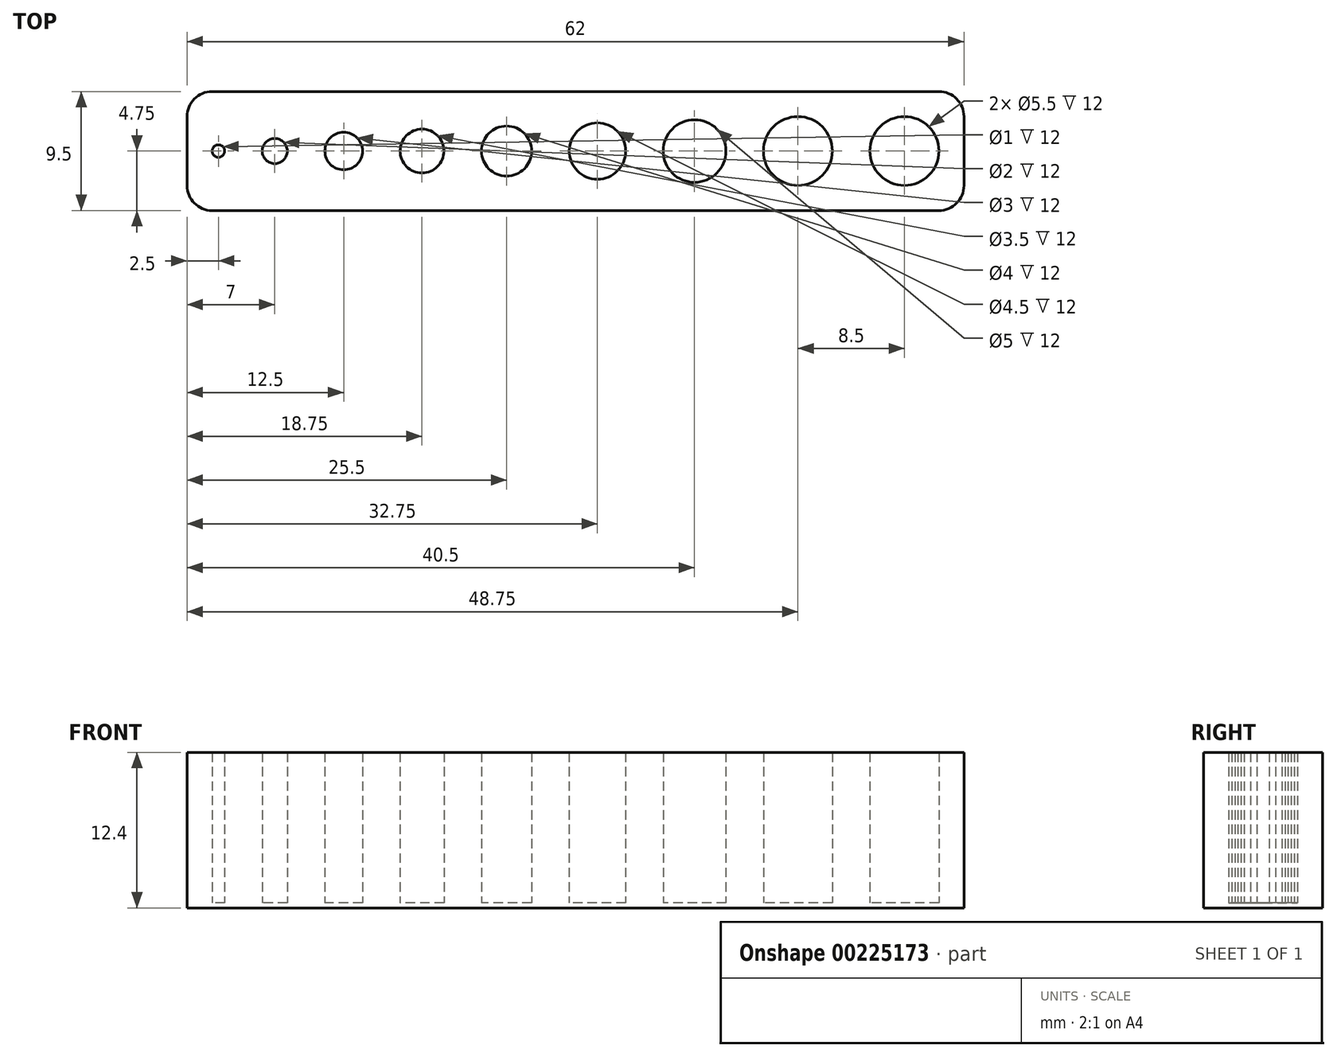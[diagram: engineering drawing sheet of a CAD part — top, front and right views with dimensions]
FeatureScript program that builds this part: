
annotation { "Feature Type Name" : "Feature", "Feature Type Description" : "" }
export const myFeature = defineFeature(function(context is Context, id is Id, definition is map)
    precondition{}
    {
        {
            var Q0;
            Q0=qCreatedBy(makeId("Top.planeOp"),FACE);
            var sketch = newSketch(context, id + "F0", { "sketchPlane" : qUnion([Q0])});
            skLineSegment(sketch, "E0.bottom", {"start": v(29.25, -4.75) * mm, "end": v(-32.75, -4.75) * mm});
            skLineSegment(sketch, "E0.top", {"start": v(29.25, 4.75) * mm, "end": v(-32.75, 4.75) * mm});
            skLineSegment(sketch, "E0.left", {"start": v(29.25, -4.75) * mm, "end": v(29.25, 4.75) * mm});
            skLineSegment(sketch, "E0.right", {"start": v(-32.75, -4.75) * mm, "end": v(-32.75, 4.75) * mm});
            skPoint(sketch, "E0.middle", {"position": v(0, 0) * mm});
            skCircle(sketch, "E1", {"center": v(-30.25, 0) * mm, "radius": 0.5 * mm});
            skCircle(sketch, "E2", {"center": v(-25.75, 0) * mm, "radius": 1 * mm});
            skCircle(sketch, "E3", {"center": v(-20.25, 0) * mm, "radius": 1.5 * mm});
            skCircle(sketch, "E4", {"center": v(-14, 0) * mm, "radius": 1.75 * mm});
            skCircle(sketch, "E5", {"center": v(-7.25, 0) * mm, "radius": 2 * mm});
            skCircle(sketch, "E6", {"center": v(0, 0) * mm, "radius": 2.25 * mm});
            skCircle(sketch, "E7", {"center": v(7.75, 0) * mm, "radius": 2.5 * mm});
            skCircle(sketch, "E8", {"center": v(16, 0) * mm, "radius": 2.75 * mm});
            skCircle(sketch, "E9", {"center": v(24.5, 0) * mm, "radius": 2.75 * mm});
            skSolve(sketch);
        }
        {
            var Q0;
            Q0=makeQuery(id+"F0.imprint","IMPRINT",FACE,{"disambiguationData":[TD([[makeQuery(id+"F0.imprint","IMPRINT",EDGE,{"derivedFrom":sQuery(id+"F0.wireOp",EDGE,"E0.bottom")}),-1.0]])]});
            extrude(context, id + "F1", {"entities" : qUnion([Q0]), "depth" : 12 * mm, "hasSecondDirection" : true, "secondDirectionOppositeDirection" : true, "secondDirectionDepth" : 0.4 * mm});
        }
        {
            var Q0;
            Q0=makeQuery(id+"F0.imprint","IMPRINT",FACE,{"disambiguationData":[TD([[makeQuery(id+"F0.imprint","IMPRINT",EDGE,{"derivedFrom":sQuery(id+"F0.wireOp",EDGE,"E2")}),1.0]])]});
            var Q1;
            Q1=makeQuery(id+"F0.imprint","IMPRINT",FACE,{"disambiguationData":[TD([[makeQuery(id+"F0.imprint","IMPRINT",EDGE,{"derivedFrom":sQuery(id+"F0.wireOp",EDGE,"E3")}),1.0]])]});
            var Q2;
            Q2=makeQuery(id+"F0.imprint","IMPRINT",FACE,{"disambiguationData":[TD([[makeQuery(id+"F0.imprint","IMPRINT",EDGE,{"derivedFrom":sQuery(id+"F0.wireOp",EDGE,"E1")}),1.0]])]});
            var Q3;
            Q3=makeQuery(id+"F0.imprint","IMPRINT",FACE,{"disambiguationData":[TD([[makeQuery(id+"F0.imprint","IMPRINT",EDGE,{"derivedFrom":sQuery(id+"F0.wireOp",EDGE,"E4")}),1.0]])]});
            var Q4;
            Q4=makeQuery(id+"F0.imprint","IMPRINT",FACE,{"disambiguationData":[TD([[makeQuery(id+"F0.imprint","IMPRINT",EDGE,{"derivedFrom":sQuery(id+"F0.wireOp",EDGE,"E5")}),1.0]])]});
            var Q5;
            Q5=makeQuery(id+"F0.imprint","IMPRINT",FACE,{"disambiguationData":[TD([[makeQuery(id+"F0.imprint","IMPRINT",EDGE,{"derivedFrom":sQuery(id+"F0.wireOp",EDGE,"E6")}),1.0]])]});
            var Q6;
            Q6=makeQuery(id+"F0.imprint","IMPRINT",FACE,{"disambiguationData":[TD([[makeQuery(id+"F0.imprint","IMPRINT",EDGE,{"derivedFrom":sQuery(id+"F0.wireOp",EDGE,"E7")}),1.0]])]});
            var Q7;
            Q7=makeQuery(id+"F0.imprint","IMPRINT",FACE,{"disambiguationData":[TD([[makeQuery(id+"F0.imprint","IMPRINT",EDGE,{"derivedFrom":sQuery(id+"F0.wireOp",EDGE,"E8")}),1.0]])]});
            var Q8;
            Q8=makeQuery(id+"F0.imprint","IMPRINT",FACE,{"disambiguationData":[TD([[makeQuery(id+"F0.imprint","IMPRINT",EDGE,{"derivedFrom":sQuery(id+"F0.wireOp",EDGE,"E9")}),1.0]])]});
            extrude(context, id + "F2", {"entities" : qUnion([Q0, Q1, Q2, Q3, Q4, Q5, Q6, Q7, Q8]), "operationType" : NewBodyOperationType.ADD, "oppositeDirection" : true, "depth" : 0.4 * mm});
        }
        {
            var Q0;
            Q0=makeQuery(id+"F1.opExtrude","SWEPT_EDGE",EDGE,{"disambiguationData":[OSD([sQuery(id+"F0.wireOp",EDGE,"E0.bottom"),sQuery(id+"F0.wireOp",EDGE,"E0.right")])]});
            var Q1;
            Q1=makeQuery(id+"F1.opExtrude","SWEPT_EDGE",EDGE,{"disambiguationData":[OSD([sQuery(id+"F0.wireOp",EDGE,"E0.bottom"),sQuery(id+"F0.wireOp",EDGE,"E0.left")])]});
            var Q2;
            Q2=makeQuery(id+"F1.opExtrude","SWEPT_EDGE",EDGE,{"disambiguationData":[OSD([sQuery(id+"F0.wireOp",EDGE,"E0.top"),sQuery(id+"F0.wireOp",EDGE,"E0.left")])]});
            var Q3;
            Q3=makeQuery(id+"F1.opExtrude","SWEPT_EDGE",EDGE,{"disambiguationData":[OSD([sQuery(id+"F0.wireOp",EDGE,"E0.top"),sQuery(id+"F0.wireOp",EDGE,"E0.right")])]});
            fillet(context, id + "F3", {"entities" : qUnion([Q0, Q1, Q2, Q3]), "radius" : 2 * mm, "tangentPropagation" : true, "allowEdgeOverflow" : false});
        }
    });
